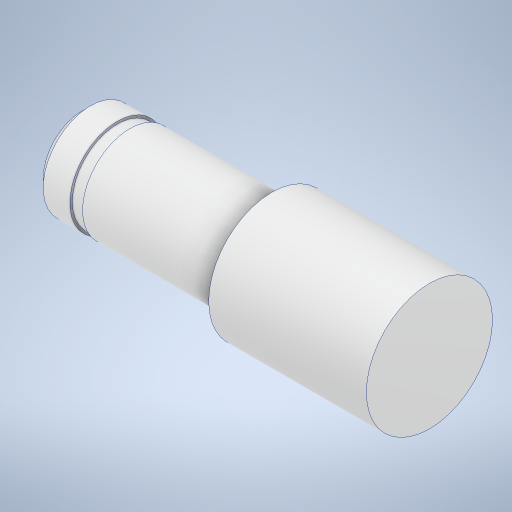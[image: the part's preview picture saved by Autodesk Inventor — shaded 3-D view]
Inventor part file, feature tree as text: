
AUTODESK INVENTOR PART (.ipt)
format: ipt  version: 2024 (Build 280153000, 153)  size: 254,976 bytes
history: native  units: mm
features: revolve x1, chamfer x1, sketch x1
ambient origin geometry x8: Origin, YZ Plane, XZ Plane, XY Plane, X Axis, Y Axis, Z Axis, Center Point
bodies: Volumenkörper1 (feature_tree)
feature tree (3):
  revolve  "Umdrehung1"
  chamfer  "Fasen1"  Distance=10.0mm
  sketch  "Skizze1"  dims[d0=22.0mm d1=10.0mm d2=9.0mm d3=0.8mm d4=8.0mm d5=6.0mm d6=5.7mm d7=90.0deg d8=0.5mm d9=2.0mm d10=45.0deg]
